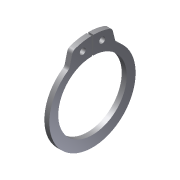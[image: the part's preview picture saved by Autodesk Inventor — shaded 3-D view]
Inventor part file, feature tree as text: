
AUTODESK INVENTOR PART (.ipt)
format: ipt  version: 2013 (Build 170138000, 138)  size: 89,600 bytes
history: native  units: in
note: dims shown in document units (in); Inventor stores cm internally (conversion verified against a paired STEP export)
features: fillet x1, other x1, imported_body x1
ambient origin geometry x8: Origin, YZ Plane, XZ Plane, XY Plane, X Axis, Y Axis, Z Axis, Center Point
feature tree (3):
  fillet  "Fillet1"  [1 undecoded]
  other  "217-2625-018 Rev1_98541A4101"
  imported_body  "Base1"
note: 1 required parameter value undecoded (feature->parameter linkage not recoverable at this tier; creation-order binding heuristic only, values carry confidence <= 0.55)
